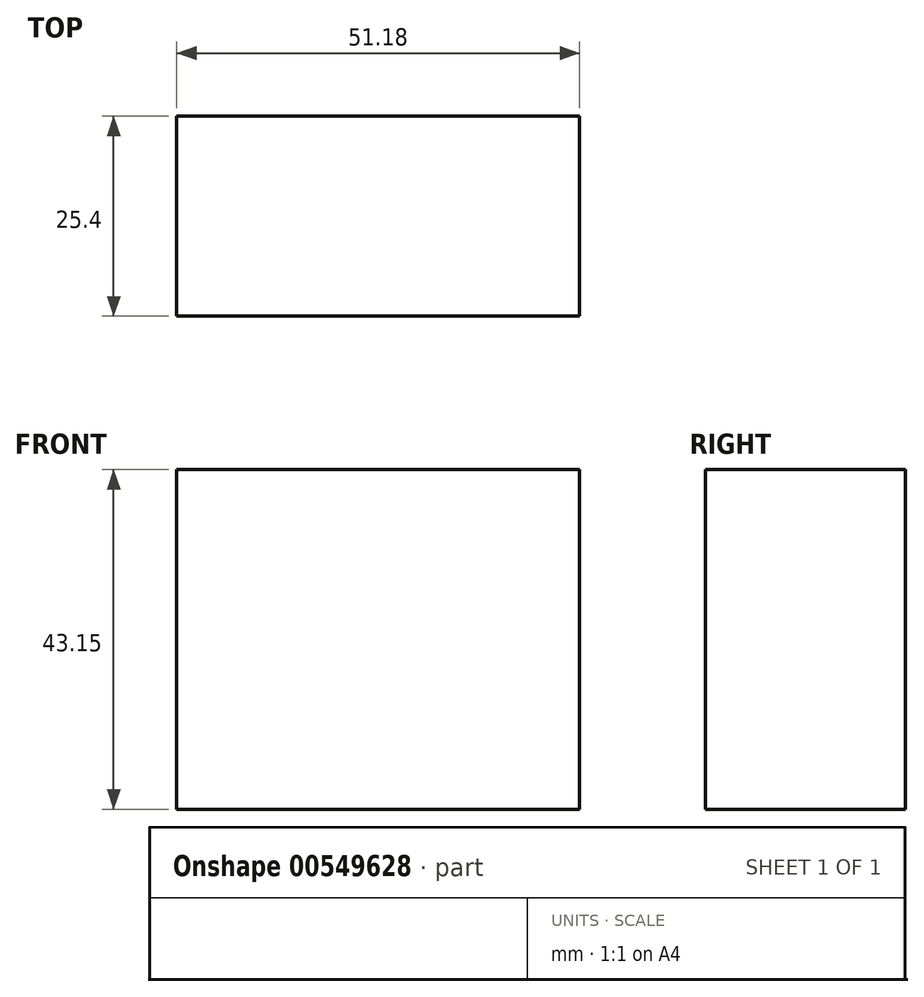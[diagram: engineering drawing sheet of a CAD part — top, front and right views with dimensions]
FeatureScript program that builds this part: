
annotation { "Feature Type Name" : "Feature", "Feature Type Description" : "" }
export const myFeature = defineFeature(function(context is Context, id is Id, definition is map)
    precondition{}
    {
        {
            var Q0;
            Q0=qCreatedBy(makeId("Front.planeOp"),FACE);
            var sketch = newSketch(context, id + "F0", { "sketchPlane" : qUnion([Q0])});
            skLineSegment(sketch, "E0.bottom", {"start": v(-110.9, 51.68) * mm, "end": v(-59.71, 51.68) * mm});
            skLineSegment(sketch, "E0.top", {"start": v(-110.9, 8.53) * mm, "end": v(-59.71, 8.53) * mm});
            skLineSegment(sketch, "E0.left", {"start": v(-110.9, 51.68) * mm, "end": v(-110.9, 8.53) * mm});
            skLineSegment(sketch, "E0.right", {"start": v(-59.71, 51.68) * mm, "end": v(-59.71, 8.53) * mm});
            skFitSpline(sketch, "E1", {"points": [v(22.58, 17.56) * mm, v(36.63, 32.87) * mm, v(43.65, 31.11) * mm, v(85.8, 11.8) * mm, v(93.58, 26.34) * mm], "startDerivative": vector(63.23, 80.46) * mm, "endDerivative": vector(13.17, 91.5) * mm});
            skSolve(sketch);
        }
        {
            var Q0;
            Q0=makeQuery(id+"F0.imprint","IMPRINT",FACE,{"disambiguationData":[TD([[makeQuery(id+"F0.imprint","IMPRINT",EDGE,{"derivedFrom":sQuery(id+"F0.wireOp",EDGE,"E0.bottom")}),-1.0]])]});
            extrude(context, id + "F1", {"entities" : qUnion([Q0]), "depth" : 25.4 * mm, "offsetDistance" : 25.4 * mm});
        }
        {
            var Q0;
            Q0=sQuery(id+"F0.wireOp",EDGE,"E1");
            extrude(context, id + "F2", {"bodyType" : ToolBodyType.SURFACE, "surfaceEntities" : qUnion([Q0]), "depth" : 25.4 * mm, "offsetDistance" : 25.4 * mm});
        }
    });
